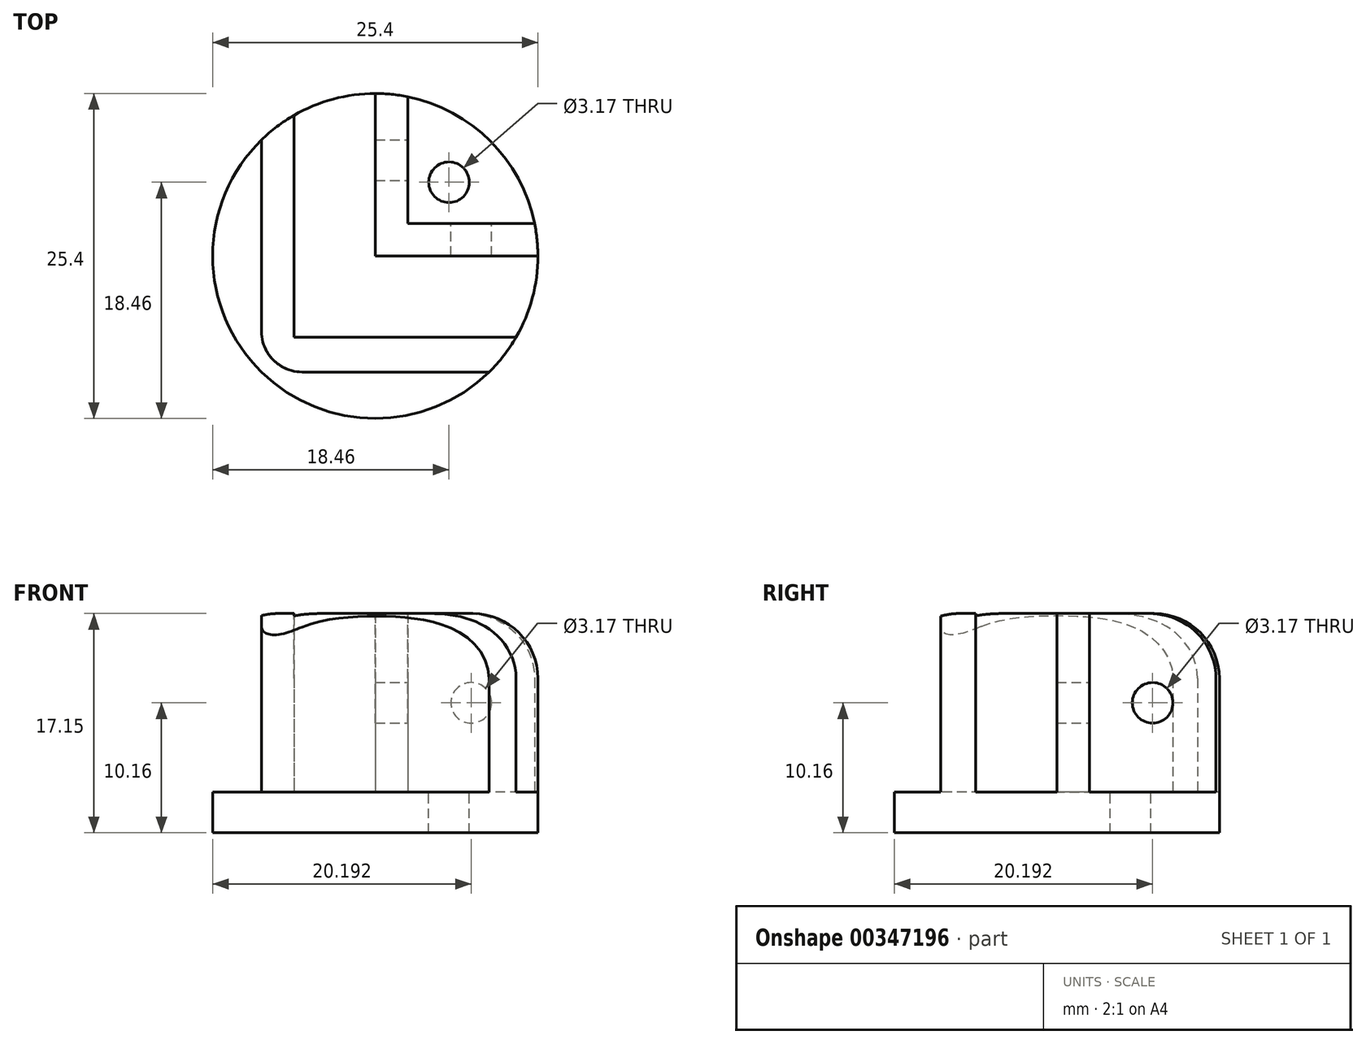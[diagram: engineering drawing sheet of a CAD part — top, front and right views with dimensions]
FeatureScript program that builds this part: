
annotation { "Feature Type Name" : "Feature", "Feature Type Description" : "" }
export const myFeature = defineFeature(function(context is Context, id is Id, definition is map)
    precondition{}
    {
        {
            var Q0;
            Q0=qCreatedBy(makeId("Top.planeOp"),FACE);
            var sketch = newSketch(context, id + "F0", { "sketchPlane" : qUnion([Q0])});
            skCircle(sketch, "E0", {"center": v(0, 0) * mm, "radius": 12.7 * mm});
            skLineSegment(sketch, "E1.bottom", {"start": v(8.89, -9.07) * mm, "end": v(-8.9, -9.07) * mm});
            skLineSegment(sketch, "E1.right", {"start": v(-8.9, -9.07) * mm, "end": v(-8.89, 9.07) * mm});
            skLineSegment(sketch, "E2", {"start": v(-6.35, 11) * mm, "end": v(-6.35, -6.35) * mm});
            skLineSegment(sketch, "E3", {"start": v(-6.35, -6.35) * mm, "end": v(11, -6.35) * mm});
            skLineSegment(sketch, "E4", {"start": v(2.54, 12.44) * mm, "end": v(2.54, 2.54) * mm});
            skLineSegment(sketch, "E5", {"start": v(2.54, 2.54) * mm, "end": v(12.44, 2.54) * mm});
            skLineSegment(sketch, "E6", {"start": v(0, 12.7) * mm, "end": v(0, 0) * mm});
            skLineSegment(sketch, "E7", {"start": v(0, 0) * mm, "end": v(12.7, 0) * mm});
            skSolve(sketch);
        }
        {
            var Q0;
            {var subQ0=sQuery(id+"F0.wireOp",EDGE,"E1.bottom");Q0=makeQuery(id+"F0.imprint","IMPRINT",FACE,{"disambiguationData":[TD([[makeQuery(id+"F0.imprint","IMPRINT",EDGE,{"derivedFrom":subQ0}),1.0]])]});}
            var Q1;
            {var subQ0=sQuery(id+"F0.wireOp",EDGE,"E1.right");Q1=makeQuery(id+"F0.imprint","IMPRINT",FACE,{"disambiguationData":[TD([[makeQuery(id+"F0.imprint","IMPRINT",EDGE,{"derivedFrom":subQ0}),1.0]])]});}
            var Q2;
            {var subQ1=sQuery(id+"F0.wireOp",EDGE,"E2");Q2=makeQuery(id+"F0.imprint","IMPRINT",FACE,{"disambiguationData":[TD([[makeQuery(id+"F0.imprint","IMPRINT",EDGE,{"derivedFrom":subQ1}),1.0]])]});}
            var Q3;
            {var subQ0=sQuery(id+"F0.wireOp",EDGE,"E4");Q3=makeQuery(id+"F0.imprint","IMPRINT",FACE,{"disambiguationData":[TD([[makeQuery(id+"F0.imprint","IMPRINT",EDGE,{"derivedFrom":subQ0}),1.0]])]});}
            extrude(context, id + "F1", {"entities" : qUnion([Q0, Q1, Q2, Q3]), "depth" : 3.17 * mm});
        }
        {
            var Q0;
            {var subQ1=sQuery(id+"F0.wireOp",EDGE,"E1.bottom");Q0=makeQuery(id+"F0.imprint","IMPRINT",FACE,{"disambiguationData":[TD([[makeQuery(id+"F0.imprint","IMPRINT",EDGE,{"derivedFrom":subQ1}),-1.0]])]});}
            var Q1;
            {var subQ1=sQuery(id+"F0.wireOp",EDGE,"E4");Q1=makeQuery(id+"F0.imprint","IMPRINT",FACE,{"disambiguationData":[TD([[makeQuery(id+"F0.imprint","IMPRINT",EDGE,{"derivedFrom":subQ1}),-1.0]])]});}
            extrude(context, id + "F2", {"entities" : qUnion([Q0, Q1]), "operationType" : NewBodyOperationType.ADD, "depth" : 17.14 * mm});
        }
        {
            var Q0;
            Q0=makeQuery(id+"F2.opExtrude","SWEPT_FACE",FACE,{"disambiguationData":[OSD([sQuery(id+"F0.wireOp",EDGE,"E5")])]});
            var sketch = newSketch(context, id + "F3", { "sketchPlane" : qUnion([Q0])});
            skCircle(sketch, "E8", {"center": v(-7.5, 10.16) * mm, "radius": 1.59 * mm});
            skPoint(sketch, "E8.centerSnap0", {"position": v(-7.5, 17.15) * mm});
            skPoint(sketch, "E8.centerSnap1", {"position": v(-12.44, 10.16) * mm});
            skSolve(sketch);
        }
        {
            var Q0;
            Q0=makeQuery(id+"F3.imprint","IMPRINT",FACE,{"disambiguationData":[TD([[makeQuery(id+"F3.imprint","IMPRINT",EDGE,{"derivedFrom":sQuery(id+"F3.wireOp",EDGE,"E8")}),1.0]])]});
            extrude(context, id + "F4", {"entities" : qUnion([Q0]), "operationType" : NewBodyOperationType.REMOVE, "endBound" : BoundingType.UP_TO_NEXT, "oppositeDirection" : true, "depth" : 25.4 * mm});
        }
        {
            var Q0;
            Q0=makeQuery(id+"F2.opExtrude","SWEPT_FACE",FACE,{"disambiguationData":[OSD([sQuery(id+"F0.wireOp",EDGE,"E4")])]});
            var sketch = newSketch(context, id + "F5", { "sketchPlane" : qUnion([Q0])});
            skCircle(sketch, "E9", {"center": v(7.5, 10.16) * mm, "radius": 1.59 * mm});
            skPoint(sketch, "E9.centerSnap0", {"position": v(7.5, 17.15) * mm});
            skPoint(sketch, "E9.centerSnap1", {"position": v(12.44, 10.16) * mm});
            skSolve(sketch);
        }
        {
            var Q0;
            Q0=makeQuery(id+"F5.imprint","IMPRINT",FACE,{"disambiguationData":[TD([[makeQuery(id+"F5.imprint","IMPRINT",EDGE,{"derivedFrom":sQuery(id+"F5.wireOp",EDGE,"E9")}),1.0]])]});
            extrude(context, id + "F6", {"entities" : qUnion([Q0]), "operationType" : NewBodyOperationType.REMOVE, "endBound" : BoundingType.UP_TO_NEXT, "oppositeDirection" : true, "depth" : 25.4 * mm});
        }
        {
            var Q0;
            Q0=makeQuery(id+"F1.opExtrude","CAP_FACE",FACE,{"disambiguationData":[OSD([sQuery(id+"F0.wireOp",EDGE,"E0"),sQuery(id+"F0.wireOp",EDGE,"E4"),sQuery(id+"F0.wireOp",EDGE,"E5")])],"isStart":false});
            var sketch = newSketch(context, id + "F7", { "sketchPlane" : qUnion([Q0])});
            skLineSegment(sketch, "E10.0", {"start": v(2.54, 2.54) * mm, "end": v(12.44, 2.54) * mm});
            skLineSegment(sketch, "E11.0", {"start": v(2.54, 12.44) * mm, "end": v(2.54, 2.54) * mm});
            skLineSegment(sketch, "E12", {"start": v(8.98, 8.98) * mm, "end": v(2.54, 2.54) * mm});
            skCircle(sketch, "E13", {"center": v(5.76, 5.76) * mm, "radius": 1.59 * mm});
            skSolve(sketch);
        }
        {
            var Q0;
            {var subQ0=sQuery(id+"F7.wireOp",EDGE,"E13");var subQ1=sQuery(id+"F7.wireOp",EDGE,"E12");var subQ2=makeQuery(id+"F7.imprint","INTERSECT",VERTEX,{"disambiguationData":[OD(0.0)],"derivedFrom":[subQ1,subQ0]});Q0=makeQuery(id+"F7.imprint","IMPRINT",FACE,{"disambiguationData":[TD([[makeQuery(id+"F7.imprint","IMPRINT",EDGE,{"disambiguationData":[TD([[subQ2,-1.0]])],"derivedFrom":subQ1}),1.0]])]});}
            var Q1;
            {var subQ0=sQuery(id+"F7.wireOp",EDGE,"E13");var subQ1=sQuery(id+"F7.wireOp",EDGE,"E12");var subQ2=makeQuery(id+"F7.imprint","INTERSECT",VERTEX,{"disambiguationData":[OD(0.0)],"derivedFrom":[subQ1,subQ0]});Q1=makeQuery(id+"F7.imprint","IMPRINT",FACE,{"disambiguationData":[TD([[makeQuery(id+"F7.imprint","IMPRINT",EDGE,{"disambiguationData":[TD([[subQ2,-1.0]])],"derivedFrom":subQ1}),-1.0]])]});}
            extrude(context, id + "F8", {"entities" : qUnion([Q0, Q1]), "operationType" : NewBodyOperationType.REMOVE, "oppositeDirection" : true, "depth" : 25.4 * mm});
        }
        {
            var Q0;
            {var subQ0=sQuery(id+"F0.wireOp",EDGE,"E0");Q0=makeQuery(id+"F2.opExtrude","CAP_EDGE",EDGE,{"disambiguationData":[OSD([subQ0]),TDD([makeQuery(id+"F0.imprint","IMPRINT",EDGE,{"disambiguationData":[TD([[makeQuery(id+"F0.imprint","INTERSECT",VERTEX,{"derivedFrom":[subQ0,sQuery(id+"F0.wireOp",EDGE,"E5")]}),1.0]])],"derivedFrom":subQ0})])],"isStart":false});}
            var Q1;
            {var subQ0=sQuery(id+"F0.wireOp",EDGE,"E0");Q1=makeQuery(id+"F2.opExtrude","CAP_EDGE",EDGE,{"disambiguationData":[OSD([subQ0]),TDD([makeQuery(id+"F0.imprint","IMPRINT",EDGE,{"disambiguationData":[TD([[makeQuery(id+"F0.imprint","INTERSECT",VERTEX,{"derivedFrom":[subQ0,sQuery(id+"F0.wireOp",EDGE,"E4")]}),-1.0]])],"derivedFrom":subQ0})])],"isStart":false});}
            var Q2;
            {var subQ0=sQuery(id+"F0.wireOp",EDGE,"E0");Q2=makeQuery(id+"F2.opExtrude","CAP_EDGE",EDGE,{"disambiguationData":[OSD([subQ0]),TDD([makeQuery(id+"F0.imprint","IMPRINT",EDGE,{"disambiguationData":[TD([[makeQuery(id+"F0.imprint","INTERSECT",VERTEX,{"derivedFrom":[subQ0,sQuery(id+"F0.wireOp",EDGE,"E1.right")]}),1.0]])],"derivedFrom":subQ0})])],"isStart":false});}
            fillet(context, id + "F9", {"entities" : qUnion([Q0, Q1, Q2]), "radius" : 5.08 * mm, "tangentPropagation" : true, "allowEdgeOverflow" : false});
        }
        {
            var Q0;
            Q0=makeQuery(id+"F2.opExtrude","SWEPT_EDGE",EDGE,{"disambiguationData":[OSD([sQuery(id+"F0.wireOp",EDGE,"E0"),sQuery(id+"F0.wireOp",EDGE,"E1.bottom"),sQuery(id+"F0.wireOp",EDGE,"E1.right")])]});
            fillet(context, id + "F10", {"entities" : qUnion([Q0]), "radius" : 3.17 * mm, "tangentPropagation" : true, "allowEdgeOverflow" : false});
        }
    });
